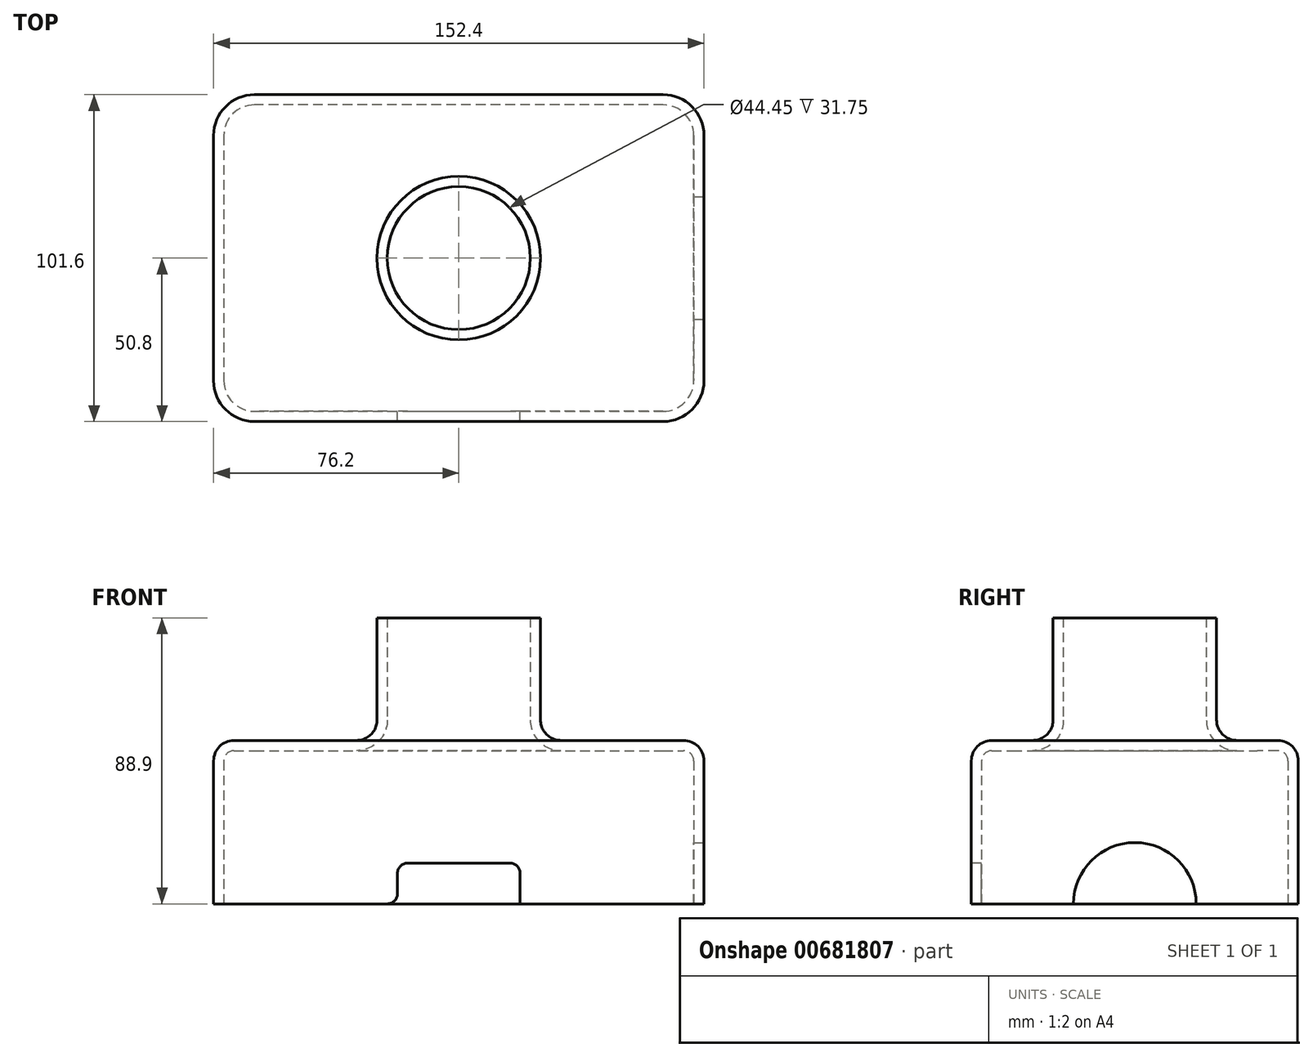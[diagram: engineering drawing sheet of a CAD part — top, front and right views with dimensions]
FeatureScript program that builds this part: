
annotation { "Feature Type Name" : "Feature", "Feature Type Description" : "" }
export const myFeature = defineFeature(function(context is Context, id is Id, definition is map)
    precondition{}
    {
        {
            var Q0;
            Q0=qCreatedBy(makeId("Top.planeOp"),FACE);
            var sketch = newSketch(context, id + "F0", { "sketchPlane" : qUnion([Q0])});
            skLineSegment(sketch, "E0.bottom", {"start": v(76.2, 50.8) * mm, "end": v(-76.2, 50.8) * mm});
            skLineSegment(sketch, "E0.top", {"start": v(76.2, -50.8) * mm, "end": v(-76.2, -50.8) * mm});
            skLineSegment(sketch, "E0.left", {"start": v(76.2, 50.8) * mm, "end": v(76.2, -50.8) * mm});
            skLineSegment(sketch, "E0.right", {"start": v(-76.2, 50.8) * mm, "end": v(-76.2, -50.8) * mm});
            skPoint(sketch, "E0.middle", {"position": v(0, 0) * mm});
            skSolve(sketch);
        }
        {
            var Q0;
            Q0=makeQuery(id+"F0.imprint","IMPRINT",FACE,{"disambiguationData":[TD([[makeQuery(id+"F0.imprint","IMPRINT",EDGE,{"derivedFrom":sQuery(id+"F0.wireOp",EDGE,"E0.bottom")}),1.0]])]});
            extrude(context, id + "F1", {"entities" : qUnion([Q0]), "depth" : 50.8 * mm, "offsetDistance" : 25.4 * mm});
        }
        {
            var Q0;
            Q0=makeQuery(id+"F1.opExtrude","CAP_FACE",FACE,{"disambiguationData":[OSD([sQuery(id+"F0.wireOp",EDGE,"E0.bottom"),sQuery(id+"F0.wireOp",EDGE,"E0.top"),sQuery(id+"F0.wireOp",EDGE,"E0.left"),sQuery(id+"F0.wireOp",EDGE,"E0.right")])],"isStart":false});
            var sketch = newSketch(context, id + "F2", { "sketchPlane" : qUnion([Q0])});
            skCircle(sketch, "E1", {"center": v(0, 0) * mm, "radius": 25.4 * mm});
            skSolve(sketch);
        }
        {
            var Q0;
            Q0=makeQuery(id+"F2.imprint","IMPRINT",FACE,{"disambiguationData":[TD([[makeQuery(id+"F2.imprint","IMPRINT",EDGE,{"derivedFrom":sQuery(id+"F2.wireOp",EDGE,"E1")}),1.0]])]});
            extrude(context, id + "F3", {"entities" : qUnion([Q0]), "operationType" : NewBodyOperationType.ADD, "depth" : 38.1 * mm, "offsetDistance" : 25.4 * mm});
        }
        {
            var Q0;
            Q0=makeQuery(id+"F1.opExtrude","SWEPT_EDGE",EDGE,{"disambiguationData":[OSD([sQuery(id+"F0.wireOp",EDGE,"E0.top"),sQuery(id+"F0.wireOp",EDGE,"E0.right")])]});
            var Q1;
            Q1=makeQuery(id+"F1.opExtrude","SWEPT_EDGE",EDGE,{"disambiguationData":[OSD([sQuery(id+"F0.wireOp",EDGE,"E0.top"),sQuery(id+"F0.wireOp",EDGE,"E0.left")])]});
            var Q2;
            Q2=makeQuery(id+"F1.opExtrude","SWEPT_EDGE",EDGE,{"disambiguationData":[OSD([sQuery(id+"F0.wireOp",EDGE,"E0.bottom"),sQuery(id+"F0.wireOp",EDGE,"E0.left")])]});
            var Q3;
            Q3=makeQuery(id+"F1.opExtrude","SWEPT_EDGE",EDGE,{"disambiguationData":[OSD([sQuery(id+"F0.wireOp",EDGE,"E0.bottom"),sQuery(id+"F0.wireOp",EDGE,"E0.right")])]});
            fillet(context, id + "F4", {"entities" : qUnion([Q0, Q1, Q2, Q3]), "radius" : 12.7 * mm, "tangentPropagation" : true, "allowEdgeOverflow" : false});
        }
        {
            var Q0;
            Q0=makeQuery(id+"F3.opExtrude","CAP_EDGE",EDGE,{"disambiguationData":[OSD([sQuery(id+"F2.wireOp",EDGE,"E1")])],"isStart":true});
            var Q1;
            Q1=makeQuery(id+"F1.opExtrude","CAP_FACE",FACE,{"disambiguationData":[OSD([sQuery(id+"F0.wireOp",EDGE,"E0.bottom"),sQuery(id+"F0.wireOp",EDGE,"E0.top"),sQuery(id+"F0.wireOp",EDGE,"E0.left"),sQuery(id+"F0.wireOp",EDGE,"E0.right")])],"isStart":false});
            fillet(context, id + "F5", {"entities" : qUnion([Q0, Q1]), "radius" : 6.35 * mm, "tangentPropagation" : true, "allowEdgeOverflow" : false});
        }
        {
            var Q0;
            Q0=makeQuery(id+"F1.opExtrude","CAP_FACE",FACE,{"disambiguationData":[OSD([sQuery(id+"F0.wireOp",EDGE,"E0.bottom"),sQuery(id+"F0.wireOp",EDGE,"E0.top"),sQuery(id+"F0.wireOp",EDGE,"E0.left"),sQuery(id+"F0.wireOp",EDGE,"E0.right")])],"isStart":true});
            var Q1;
            Q1=makeQuery(id+"F3.opExtrude","CAP_FACE",FACE,{"disambiguationData":[OSD([sQuery(id+"F2.wireOp",EDGE,"E1")])],"isStart":false});
            shell(context, id + "F6", {"entities" : qUnion([Q0, Q1]), "thickness" : 3.17 * mm});
        }
        {
            var Q0;
            Q0=makeQuery(id+"F1.opExtrude","SWEPT_FACE",FACE,{"disambiguationData":[OSD([sQuery(id+"F0.wireOp",EDGE,"E0.left")])]});
            var sketch = newSketch(context, id + "F7", { "sketchPlane" : qUnion([Q0])});
            skCircle(sketch, "E2", {"center": v(0, 0) * mm, "radius": 19.05 * mm});
            skSolve(sketch);
        }
        {
            var Q0;
            {var subQ0=sQuery(id+"F7.wireOp",EDGE,"E2");var subQ1=makeQuery(id+"F1.opExtrude","CAP_EDGE",EDGE,{"disambiguationData":[OSD([sQuery(id+"F0.wireOp",EDGE,"E0.left")])],"isStart":true});var subQ2=makeQuery(id+"F7.imprint","INTERSECT",VERTEX,{"disambiguationData":[OD(0.0)],"derivedFrom":[subQ1,subQ0]});Q0=makeQuery(id+"F7.imprint","IMPRINT",FACE,{"disambiguationData":[TD([[makeQuery(id+"F7.imprint","IMPRINT",EDGE,{"disambiguationData":[TD([[subQ2,-1.0]])],"derivedFrom":subQ0}),1.0]])]});}
            extrude(context, id + "F8", {"entities" : qUnion([Q0]), "operationType" : NewBodyOperationType.REMOVE, "endBound" : BoundingType.UP_TO_NEXT, "oppositeDirection" : true, "depth" : 25.4 * mm, "offsetDistance" : 25.4 * mm});
        }
        {
            var Q0;
            Q0=makeQuery(id+"F1.opExtrude","SWEPT_FACE",FACE,{"disambiguationData":[OSD([sQuery(id+"F0.wireOp",EDGE,"E0.top")])]});
            var sketch = newSketch(context, id + "F9", { "sketchPlane" : qUnion([Q0])});
            skLineSegment(sketch, "E3.bottom", {"start": v(19.05, 12.7) * mm, "end": v(-19.05, 12.7) * mm});
            skLineSegment(sketch, "E3.top", {"start": v(19.05, -12.7) * mm, "end": v(-19.05, -12.7) * mm});
            skLineSegment(sketch, "E3.left", {"start": v(19.05, 12.7) * mm, "end": v(19.05, -12.7) * mm});
            skLineSegment(sketch, "E3.right", {"start": v(-19.05, 12.7) * mm, "end": v(-19.05, -12.7) * mm});
            skPoint(sketch, "E3.middle", {"position": v(0, 0) * mm});
            skSolve(sketch);
        }
        {
            var Q0;
            Q0 = qSketchRegion(id + "F9", true);
            extrude(context, id + "F10", {"entities" : qUnion([Q0]), "operationType" : NewBodyOperationType.REMOVE, "endBound" : BoundingType.UP_TO_NEXT, "oppositeDirection" : true, "depth" : 25.4 * mm, "offsetDistance" : 25.4 * mm});
        }
        {
            var Q0;
            Q0=makeQuery(id+"F10.boolean.opBoolean","COPY",EDGE,{"derivedFrom":makeQuery(id+"F10.opExtrude","SWEPT_EDGE",EDGE,{"disambiguationData":[OSD([sQuery(id+"F9.wireOp",EDGE,"E3.bottom"),sQuery(id+"F9.wireOp",EDGE,"E3.right")])]})});
            var Q1;
            Q1=makeQuery(id+"F10.boolean.opBoolean","COPY",EDGE,{"derivedFrom":makeQuery(id+"F10.opExtrude","CAP_EDGE",EDGE,{"disambiguationData":[OSD([sQuery(id+"F9.wireOp",EDGE,"E3.right")]),topologyDisambiguationEdgeConnected([makeQuery(id+"F1.opExtrude","CAP_FACE",FACE,{"disambiguationData":[OSD([sQuery(id+"F0.wireOp",EDGE,"E0.bottom"),sQuery(id+"F0.wireOp",EDGE,"E0.top"),sQuery(id+"F0.wireOp",EDGE,"E0.left"),sQuery(id+"F0.wireOp",EDGE,"E0.right")])],"isStart":true})])],"isStart":false})});
            var Q2;
            Q2=makeQuery(id+"F10.boolean.opBoolean","COPY",EDGE,{"derivedFrom":makeQuery(id+"F10.opExtrude","SWEPT_EDGE",EDGE,{"disambiguationData":[OSD([sQuery(id+"F9.wireOp",EDGE,"E3.bottom"),sQuery(id+"F9.wireOp",EDGE,"E3.left")])]})});
            var Q3;
            Q3=makeQuery(id+"F10.boolean.opBoolean","COPY",EDGE,{"derivedFrom":makeQuery(id+"F10.opExtrude","CAP_EDGE",EDGE,{"disambiguationData":[OSD([sQuery(id+"F9.wireOp",EDGE,"E3.left")]),topologyDisambiguationEdgeConnected([makeQuery(id+"F1.opExtrude","CAP_FACE",FACE,{"disambiguationData":[OSD([sQuery(id+"F0.wireOp",EDGE,"E0.bottom"),sQuery(id+"F0.wireOp",EDGE,"E0.top"),sQuery(id+"F0.wireOp",EDGE,"E0.left"),sQuery(id+"F0.wireOp",EDGE,"E0.right")])],"isStart":true})])],"isStart":false})});
            var Q4;
            {var subQ0=sQuery(id+"F7.wireOp",EDGE,"E2");var subQ1=sQuery(id+"F0.wireOp",EDGE,"E0.left");Q4=makeQuery(id+"F8.boolean.opBoolean","COPY",EDGE,{"derivedFrom":makeQuery(id+"F8.opExtrude","SWEPT_EDGE",EDGE,{"disambiguationData":[OSD([subQ1,subQ0]),TDD([makeQuery(id+"F7.imprint","INTERSECT",VERTEX,{"disambiguationData":[OD(1.0)],"derivedFrom":[makeQuery(id+"F1.opExtrude","CAP_EDGE",EDGE,{"disambiguationData":[OSD([subQ1])],"isStart":true}),subQ0]})])]})});}
            var Q5;
            {var subQ0=sQuery(id+"F7.wireOp",EDGE,"E2");var subQ1=sQuery(id+"F0.wireOp",EDGE,"E0.left");Q5=makeQuery(id+"F8.boolean.opBoolean","COPY",EDGE,{"derivedFrom":makeQuery(id+"F8.opExtrude","SWEPT_EDGE",EDGE,{"disambiguationData":[OSD([subQ1,subQ0]),TDD([makeQuery(id+"F7.imprint","INTERSECT",VERTEX,{"disambiguationData":[OD(0.0)],"derivedFrom":[makeQuery(id+"F1.opExtrude","CAP_EDGE",EDGE,{"disambiguationData":[OSD([subQ1])],"isStart":true}),subQ0]})])]})});}
            fillet(context, id + "F11", {"entities" : qUnion([Q0, Q1, Q2, Q3, Q4, Q5]), "radius" : 3.17 * mm, "tangentPropagation" : true, "allowEdgeOverflow" : false});
        }
    });
